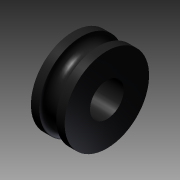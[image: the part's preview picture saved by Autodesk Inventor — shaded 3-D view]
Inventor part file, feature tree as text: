
AUTODESK INVENTOR PART (.ipt)
format: ipt  version: 2012 (Build 160160000, 160)  size: 119,296 bytes
history: native  units: in
note: dims shown in document units (in); Inventor stores cm internally (conversion verified against a paired STEP export)
features: sketch x2, revolve x1, extrude x1
ambient origin geometry x8: Origin, YZ Plane, XZ Plane, XY Plane, X Axis, Y Axis, Z Axis, Center Point
bodies: Solid1 (feature_tree)
feature tree (4):
  revolve  "Revolution1"  [1 undecoded]
  extrude  "Extrusion1"  Depth=0.125in
  sketch  "Sketch1"  dims[d0=0.5in d1=0.625in]
  sketch  "Sketch2"  dims[d2=0.125in d3=0.125in d4=90.0deg d5=0.5in d6=1.0in d7=0.0in]
note: 1 required parameter value undecoded (feature->parameter linkage not recoverable at this tier; creation-order binding heuristic only, values carry confidence <= 0.55)
